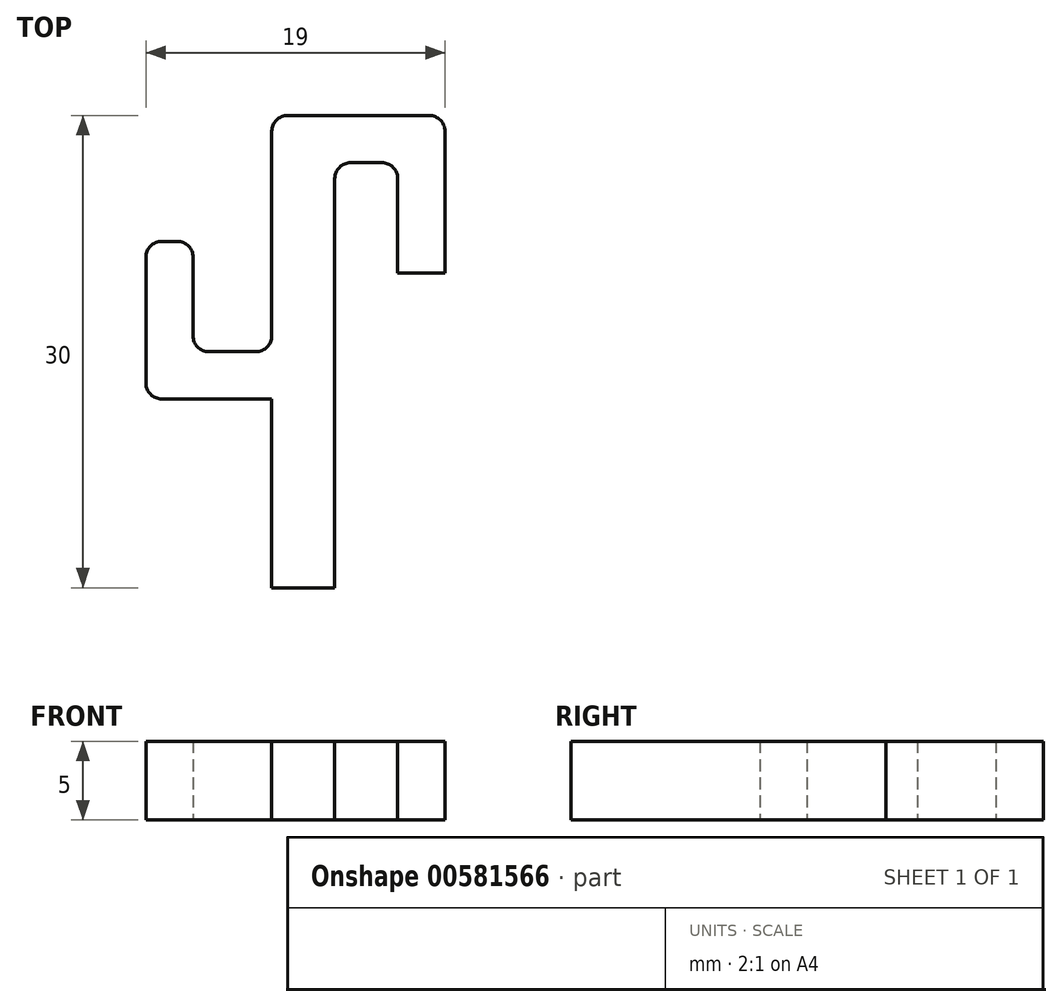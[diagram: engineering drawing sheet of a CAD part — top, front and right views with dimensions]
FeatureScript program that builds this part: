
annotation { "Feature Type Name" : "Feature", "Feature Type Description" : "" }
export const myFeature = defineFeature(function(context is Context, id is Id, definition is map)
    precondition{}
    {
        {
            var Q0;
            Q0=qCreatedBy(makeId("Top.planeOp"),FACE);
            var sketch = newSketch(context, id + "F0", { "sketchPlane" : qUnion([Q0])});
            skLineSegment(sketch, "E0", {"start": v(0, 0) * mm, "end": v(0, 9) * mm});
            skLineSegment(sketch, "E1", {"start": v(-1, 10) * mm, "end": v(-10, 10) * mm});
            skLineSegment(sketch, "E2", {"start": v(-11, 9) * mm, "end": v(-11, -4) * mm});
            skLineSegment(sketch, "E3", {"start": v(-11, -20) * mm, "end": v(-7, -20) * mm});
            skLineSegment(sketch, "E4", {"start": v(-7, -20) * mm, "end": v(-7, 6) * mm});
            skLineSegment(sketch, "E5", {"start": v(-6, 7) * mm, "end": v(-4, 7) * mm});
            skLineSegment(sketch, "E6", {"start": v(-3, 6) * mm, "end": v(-3, 0) * mm});
            skLineSegment(sketch, "E7", {"start": v(-3, 0) * mm, "end": v(0, 0) * mm});
            skPoint(sketch, "E8.oppositeSnap0", {"position": v(-11, -5) * mm});
            skLineSegment(sketch, "E8.bottom", {"start": v(-11, -8) * mm, "end": v(-18, -8) * mm});
            skLineSegment(sketch, "E8.right", {"start": v(-19, 1) * mm, "end": v(-19, -7) * mm});
            skLineSegment(sketch, "E9.trimOffspring", {"start": v(-11, -8) * mm, "end": v(-11, -20) * mm});
            skLineSegment(sketch, "E10", {"start": v(-18, 2) * mm, "end": v(-17, 2) * mm});
            skLineSegment(sketch, "E11", {"start": v(-16, 1) * mm, "end": v(-16, -4) * mm});
            skLineSegment(sketch, "E12", {"start": v(-15, -5) * mm, "end": v(-12, -5) * mm});
            skPoint(sketch, "E13.visualSharp", {"position": v(-19, -8) * mm});
            skArc(sketch, "E13.filletArc", {"start": v(-19, -7) * mm, "mid": v(-18.7, -7.7) * mm, "end": v(-18, -8) * mm});
            skPoint(sketch, "E14.visualSharp", {"position": v(-16, -5) * mm});
            skArc(sketch, "E14.filletArc", {"start": v(-16, -4) * mm, "mid": v(-15.7, -4.7) * mm, "end": v(-15, -5) * mm});
            skPoint(sketch, "E15.visualSharp", {"position": v(-19, 2) * mm});
            skArc(sketch, "E15.filletArc", {"start": v(-18, 2) * mm, "mid": v(-18.7, 1.7) * mm, "end": v(-19, 1) * mm});
            skPoint(sketch, "E16.visualSharp", {"position": v(-16, 2) * mm});
            skArc(sketch, "E16.filletArc", {"start": v(-16, 1) * mm, "mid": v(-16.3, 1.7) * mm, "end": v(-17, 2) * mm});
            skArc(sketch, "E17.filletArc", {"start": v(-12, -5) * mm, "mid": v(-11.3, -4.7) * mm, "end": v(-11, -4) * mm});
            skPoint(sketch, "E18.visualSharp", {"position": v(-3, 7) * mm});
            skArc(sketch, "E18.filletArc", {"start": v(-3, 6) * mm, "mid": v(-3.3, 6.7) * mm, "end": v(-4, 7) * mm});
            skPoint(sketch, "E19.visualSharp", {"position": v(-7, 7) * mm});
            skArc(sketch, "E19.filletArc", {"start": v(-6, 7) * mm, "mid": v(-6.7, 6.7) * mm, "end": v(-7, 6) * mm});
            skPoint(sketch, "E20.visualSharp", {"position": v(-11, 10) * mm});
            skArc(sketch, "E20.filletArc", {"start": v(-10, 10) * mm, "mid": v(-10.7, 9.7) * mm, "end": v(-11, 9) * mm});
            skPoint(sketch, "E21.visualSharp", {"position": v(0, 10) * mm});
            skArc(sketch, "E21.filletArc", {"start": v(0, 9) * mm, "mid": v(-0.3, 9.7) * mm, "end": v(-1, 10) * mm});
            skSolve(sketch);
        }
        {
            var Q0;
            Q0=makeQuery(id+"F0.imprint","IMPRINT",FACE,{"disambiguationData":[TD([[makeQuery(id+"F0.imprint","IMPRINT",EDGE,{"derivedFrom":sQuery(id+"F0.wireOp",EDGE,"E0")}),1.0]])]});
            extrude(context, id + "F1", {"entities" : qUnion([Q0]), "depth" : 5 * mm, "offsetDistance" : 25 * mm});
        }
    });
